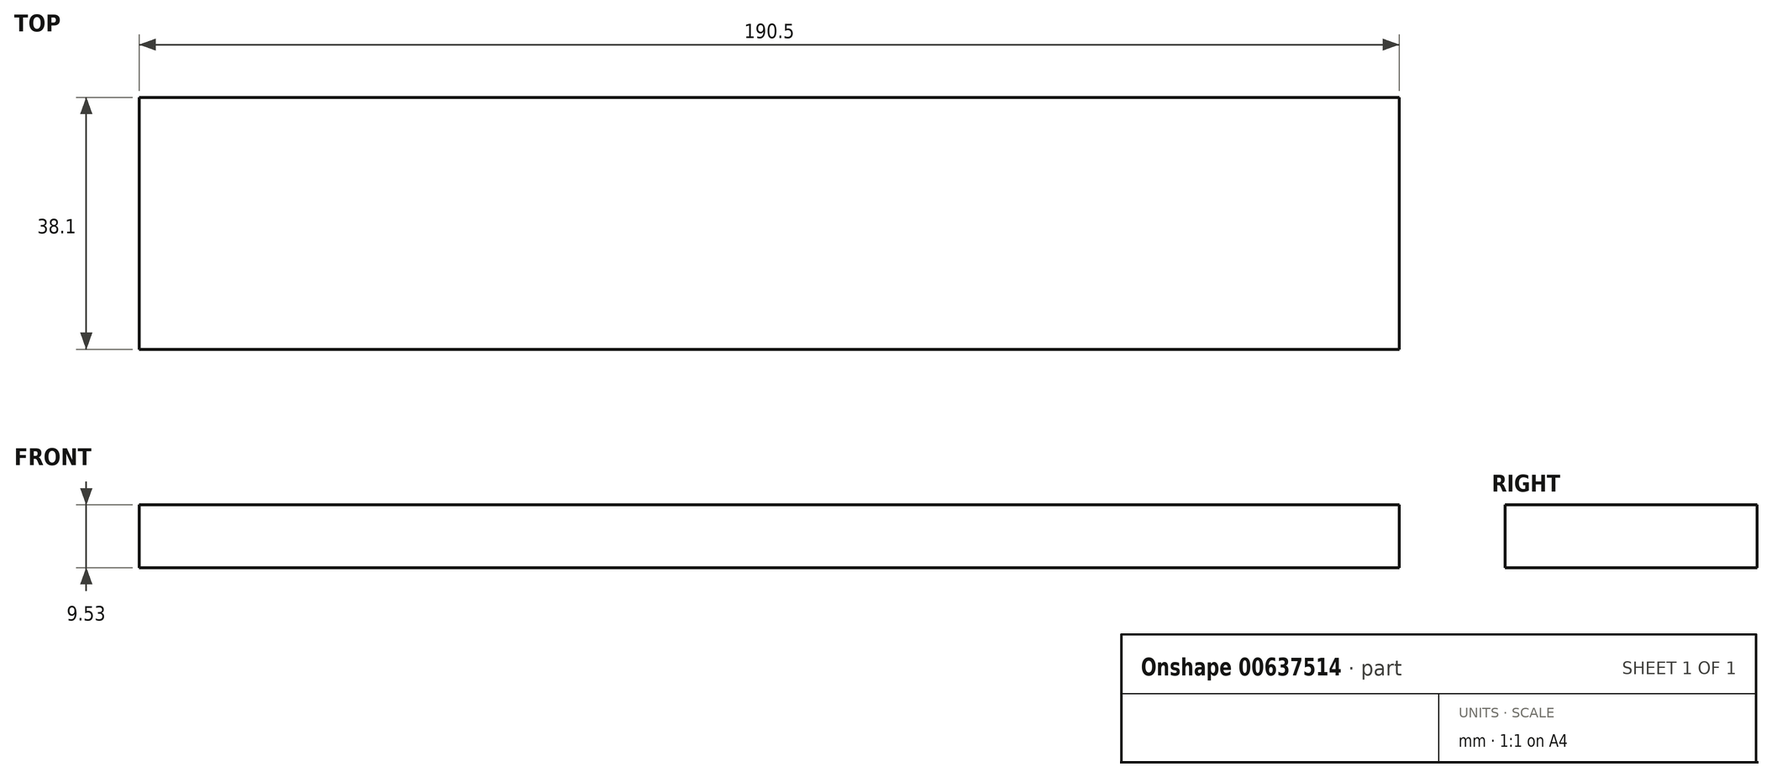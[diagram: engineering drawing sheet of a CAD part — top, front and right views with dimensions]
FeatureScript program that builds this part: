
annotation { "Feature Type Name" : "Feature", "Feature Type Description" : "" }
export const myFeature = defineFeature(function(context is Context, id is Id, definition is map)
    precondition{}
    {
        {
            var Q0;
            Q0=qCreatedBy(makeId("Top.planeOp"),FACE);
            var sketch = newSketch(context, id + "F0", { "sketchPlane" : qUnion([Q0])});
            skLineSegment(sketch, "E0.bottom", {"start": v(-39.84, 19.8) * mm, "end": v(150.66, 19.8) * mm});
            skLineSegment(sketch, "E0.top", {"start": v(-39.84, -18.3) * mm, "end": v(150.66, -18.3) * mm});
            skLineSegment(sketch, "E0.left", {"start": v(-39.84, 19.8) * mm, "end": v(-39.84, -18.3) * mm});
            skLineSegment(sketch, "E0.right", {"start": v(150.66, 19.8) * mm, "end": v(150.66, -18.3) * mm});
            skSolve(sketch);
        }
        {
            var Q0;
            Q0=makeQuery(id+"F0.imprint","IMPRINT",FACE,{"disambiguationData":[TD([[makeQuery(id+"F0.imprint","IMPRINT",EDGE,{"derivedFrom":sQuery(id+"F0.wireOp",EDGE,"E0.bottom")}),-1.0]])]});
            extrude(context, id + "F1", {"entities" : qUnion([Q0]), "depth" : 9.52 * mm, "offsetDistance" : 25.4 * mm});
        }
    });
